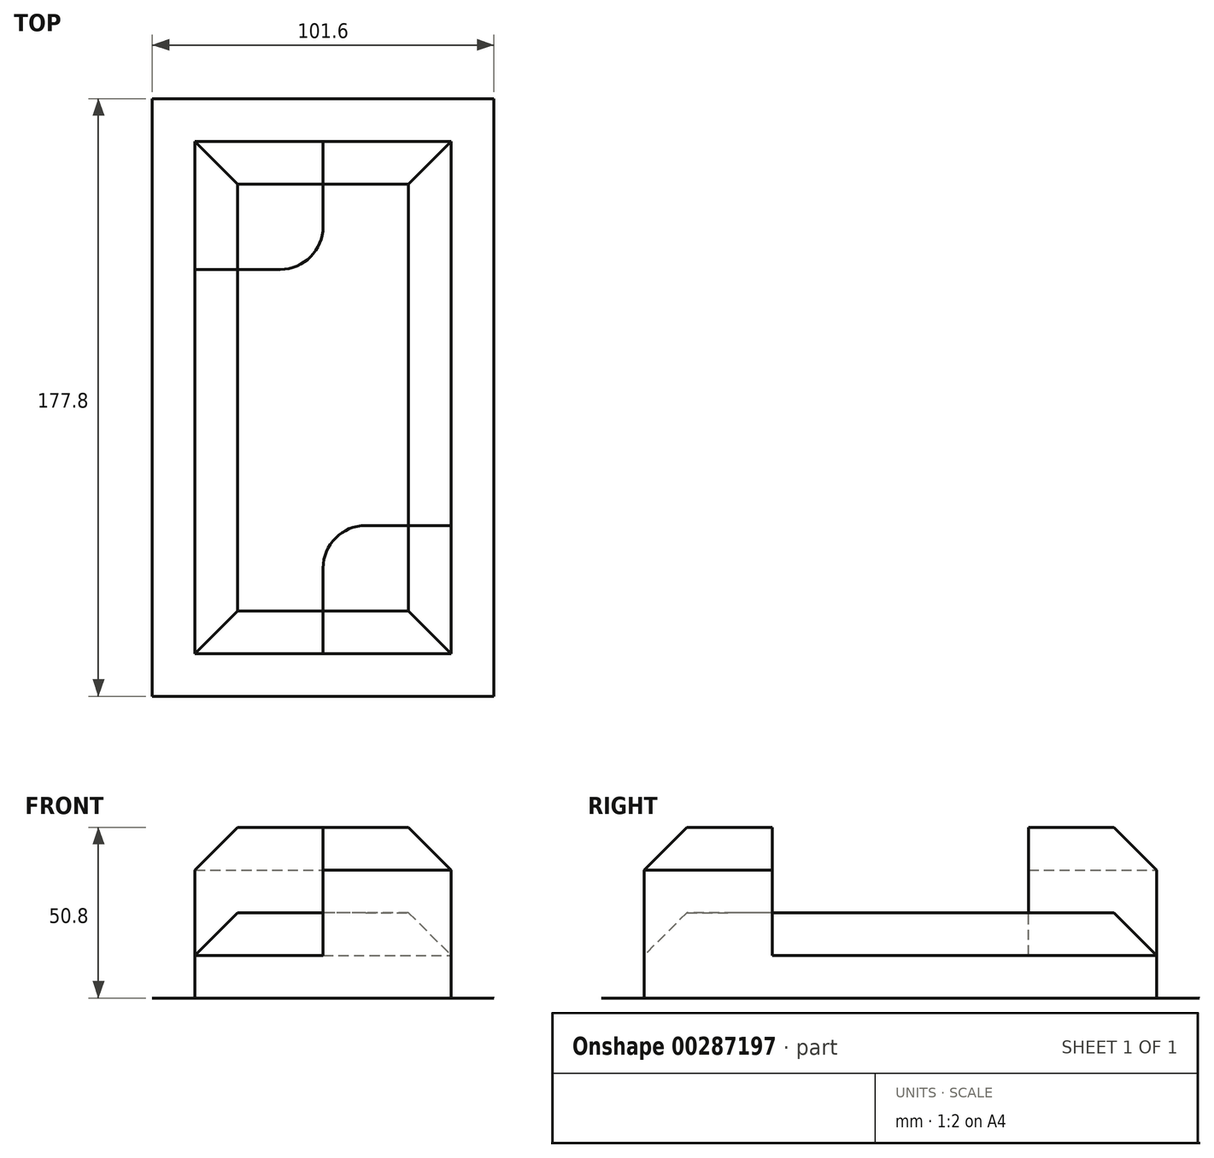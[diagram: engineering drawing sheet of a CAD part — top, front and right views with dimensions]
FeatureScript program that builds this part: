
annotation { "Feature Type Name" : "Feature", "Feature Type Description" : "" }
export const myFeature = defineFeature(function(context is Context, id is Id, definition is map)
    precondition{}
    {
        {
            var Q0;
            Q0=qCreatedBy(makeId("Top.planeOp"),FACE);
            var sketch = newSketch(context, id + "F0", { "sketchPlane" : qUnion([Q0])});
            skLineSegment(sketch, "E0.bottom", {"start": v(-31.45, 103.9) * mm, "end": v(6.65, 103.9) * mm});
            skLineSegment(sketch, "E0.top", {"start": v(-31.45, -48.5) * mm, "end": v(6.65, -48.5) * mm});
            skLineSegment(sketch, "E0.left", {"start": v(-31.45, 103.9) * mm, "end": v(-31.45, 65.8) * mm});
            skLineSegment(sketch, "E0.right", {"start": v(44.75, 103.9) * mm, "end": v(44.75, -10.4) * mm});
            skLineSegment(sketch, "E1.0", {"start": v(-44.15, 116.6) * mm, "end": v(-44.15, -61.2) * mm});
            skLineSegment(sketch, "E1.1", {"start": v(-44.15, 116.6) * mm, "end": v(57.45, 116.6) * mm});
            skLineSegment(sketch, "E1.2", {"start": v(57.45, 116.6) * mm, "end": v(57.45, -61.2) * mm});
            skLineSegment(sketch, "E1.3", {"start": v(-44.15, -61.2) * mm, "end": v(57.45, -61.2) * mm});
            skLineSegment(sketch, "E2", {"start": v(6.65, 103.9) * mm, "end": v(44.75, 103.9) * mm});
            skLineSegment(sketch, "E3", {"start": v(-31.45, 65.8) * mm, "end": v(-31.45, -48.5) * mm});
            skLineSegment(sketch, "E4", {"start": v(-31.45, 65.8) * mm, "end": v(-6.05, 65.8) * mm});
            skLineSegment(sketch, "E5", {"start": v(6.65, 103.9) * mm, "end": v(6.65, 78.5) * mm});
            skLineSegment(sketch, "E6", {"start": v(6.65, -48.5) * mm, "end": v(44.75, -48.5) * mm});
            skLineSegment(sketch, "E7", {"start": v(44.75, -10.4) * mm, "end": v(44.75, -48.5) * mm});
            skLineSegment(sketch, "E8", {"start": v(6.65, -48.5) * mm, "end": v(6.65, -23.1) * mm});
            skLineSegment(sketch, "E9", {"start": v(19.35, -10.4) * mm, "end": v(44.75, -10.4) * mm});
            skPoint(sketch, "E10.visualSharp", {"position": v(6.65, 65.8) * mm});
            skArc(sketch, "E10.filletArc", {"start": v(-6.05, 65.8) * mm, "mid": v(2.93, 69.53) * mm, "end": v(6.65, 78.5) * mm});
            skPoint(sketch, "E11.visualSharp", {"position": v(6.65, -10.4) * mm});
            skArc(sketch, "E11.filletArc", {"start": v(19.35, -10.4) * mm, "mid": v(10.37, -14.11) * mm, "end": v(6.65, -23.1) * mm});
            skSolve(sketch);
        }
        {
            var Q0;
            Q0=makeQuery(id+"F0.imprint","IMPRINT",FACE,{"disambiguationData":[TD([[makeQuery(id+"F0.imprint","IMPRINT",EDGE,{"derivedFrom":sQuery(id+"F0.wireOp",EDGE,"E0.top")}),1.0]])]});
            extrude(context, id + "F1", {"entities" : qUnion([Q0]), "depth" : 25.4 * mm});
        }
        {
            var Q0;
            Q0=makeQuery(id+"F0.imprint","IMPRINT",FACE,{"disambiguationData":[TD([[makeQuery(id+"F0.imprint","IMPRINT",EDGE,{"derivedFrom":sQuery(id+"F0.wireOp",EDGE,"E0.bottom")}),-1.0]])]});
            var Q1;
            Q1=makeQuery(id+"F0.imprint","IMPRINT",FACE,{"disambiguationData":[TD([[makeQuery(id+"F0.imprint","IMPRINT",EDGE,{"derivedFrom":sQuery(id+"F0.wireOp",EDGE,"E6")}),1.0]])]});
            extrude(context, id + "F2", {"entities" : qUnion([Q0, Q1]), "operationType" : NewBodyOperationType.ADD, "depth" : 50.8 * mm});
        }
        {
            var Q0;
            Q0=makeQuery(id+"F0.imprint","IMPRINT",FACE,{"disambiguationData":[TD([[makeQuery(id+"F0.imprint","IMPRINT",EDGE,{"derivedFrom":sQuery(id+"F0.wireOp",EDGE,"E0.bottom")}),1.0]])]});
            extrude(context, id + "F3", {"entities" : qUnion([Q0]), "operationType" : NewBodyOperationType.ADD, "depth" : 1 / 101.6 * mm});
        }
        {
            var Q0;
            Q0=makeQuery(id+"F3.opExtrude","CAP_EDGE",EDGE,{"disambiguationData":[OSD([sQuery(id+"F0.wireOp",EDGE,"E1.3")])],"isStart":false});
            var Q1;
            Q1=makeQuery(id+"F3.opExtrude","CAP_EDGE",EDGE,{"disambiguationData":[OSD([sQuery(id+"F0.wireOp",EDGE,"E1.0")])],"isStart":false});
            var Q2;
            Q2=makeQuery(id+"F3.opExtrude","CAP_EDGE",EDGE,{"disambiguationData":[OSD([sQuery(id+"F0.wireOp",EDGE,"E1.1")])],"isStart":false});
            var Q3;
            Q3=makeQuery(id+"F3.opExtrude","CAP_EDGE",EDGE,{"disambiguationData":[OSD([sQuery(id+"F0.wireOp",EDGE,"E1.2")])],"isStart":false});
            fillet(context, id + "F4", {"entities" : qUnion([Q0, Q1, Q2, Q3]), "radius" : 6.35 * mm, "tangentPropagation" : true, "allowEdgeOverflow" : false});
        }
        {
            var Q0;
            Q0=makeQuery(id+"F1.opExtrude","CAP_EDGE",EDGE,{"disambiguationData":[OSD([sQuery(id+"F0.wireOp",EDGE,"E0.top")])],"isStart":false});
            var Q1;
            Q1=makeQuery(id+"F1.opExtrude","CAP_EDGE",EDGE,{"disambiguationData":[OSD([sQuery(id+"F0.wireOp",EDGE,"E3")])],"isStart":false});
            var Q2;
            Q2=makeQuery(id+"F1.opExtrude","CAP_EDGE",EDGE,{"disambiguationData":[OSD([sQuery(id+"F0.wireOp",EDGE,"E0.right")])],"isStart":false});
            var Q3;
            Q3=makeQuery(id+"F1.opExtrude","CAP_EDGE",EDGE,{"disambiguationData":[OSD([sQuery(id+"F0.wireOp",EDGE,"E2")])],"isStart":false});
            chamfer(context, id + "F5", {"entities" : qUnion([Q0, Q1, Q2, Q3]), "width" : 12.7 * mm, "tangentPropagation" : true});
        }
        {
            var Q0;
            Q0=makeQuery(id+"F2.opExtrude","CAP_EDGE",EDGE,{"disambiguationData":[OSD([sQuery(id+"F0.wireOp",EDGE,"E7")])],"isStart":false});
            var Q1;
            Q1=makeQuery(id+"F2.opExtrude","CAP_EDGE",EDGE,{"disambiguationData":[OSD([sQuery(id+"F0.wireOp",EDGE,"E6")])],"isStart":false});
            var Q2;
            Q2=makeQuery(id+"F2.opExtrude","CAP_EDGE",EDGE,{"disambiguationData":[OSD([sQuery(id+"F0.wireOp",EDGE,"E0.left")])],"isStart":false});
            var Q3;
            Q3=makeQuery(id+"F2.opExtrude","CAP_EDGE",EDGE,{"disambiguationData":[OSD([sQuery(id+"F0.wireOp",EDGE,"E0.bottom")])],"isStart":false});
            chamfer(context, id + "F6", {"entities" : qUnion([Q0, Q1, Q2, Q3]), "width" : 12.7 * mm, "tangentPropagation" : true});
        }
    });
